# Revit family: Faucet-Deck_Mount-Bath-KOHLER-MODERN-K-97360T_2
name_source: partatom
category: Plumbing Fixtures
revit_build: Autodesk Revit 2017 (Build: 20160225_1515(x64)
units: mm (PartAtom-declared; Revit-internal decimal feet)

## family parameters
Cut with Voids When Loaded = No
Host = Face
OmniClass Number = 23.31.11.00
OmniClass Title = Faucets
Part Type = Normal
Room Calculation Point = No
Round Connector Dimension = Use Diameter
Shared = No

## types (6) — shared parameters
ADA Compliant = No
Assembly Code = D2010
CW Connection = Yes
Cold Water Inlet = Cold Water Inlet
Date Modified = 05/20/2020
Default Elevation = 36"
Drain Included = No
Flow Rate = 0 GPM
HW Connection = Yes
Handle Clearance = 3 3/8"
Height = 6 13/16"
Hot Water Inlet = Hot Water Inlet
Length = 7 13/16"
Manufacturer = KOHLER Co.
MasterFormat 1995 = 15410
MasterFormat 2004 = 22.41.39
Material = Premium Metal Construction
Pressure = 72.52 psi
Product Name = MODERN
Spout Reach = 7 13/16"
URL = http://www.kohler.com.cn
Vent Connection = No
Waste Connection = No
Waste Water Outlet = Waste Water Outlet
WaterSense Certified = No
Width = 2 9/16"

## per-type parameters (varying)
| type | Description | Finish | Height of Handshower | Model | Product Documentation Link | Product Page URL | Type |
| B4,TT-Vibrant Titanium | 3 hole cylinder side bathtub faucet | Kohler-Metal-TT-Vibrant_Titanium | 9 7/8" | K-97360T-B4-TT | http://files.kohler.com.cn | http://www.kohler.com.cn | 2 |
| 4E,CP-Polished Chrome | HOB MOUNT BATH SPOUT with Handshower | Kohler-Metal-CP-Polished_Chrome | 9 7/8" | K-97360T-4E-CP |  |  | 3 |
| 4E,TT-Vibrant Titanium | HOB MOUNT BATH SPOUT with Handshower | Kohler-Metal-TT-Vibrant_Titanium | 9 7/8" | K-97360T-4E-TT |  |  | 4 |
| B4,CP-Polished Chrome | 3 hole cylinder side bathtub faucet | Kohler-Metal-CP-Polished_Chrome | 9 7/8" | K-97360T-B4-CP | http://files.kohler.com.cn | http://www.kohler.com.cn | 1 |
| CP-Polished Chrome | HOB MOUNT BATH SPOUT with Handshower | Kohler-Metal-CP-Polished_Chrome | 9 1/8" | K-97360T-4-CP |  |  | 5 |
| TT-Vibrant Titanium | HOB MOUNT BATH SPOUT with Handshower | Kohler-Metal-TT-Vibrant_Titanium | 9 1/8" | K-97360T-4-TT |  |  | 6 |

## geometry (parser evidence)
native form markers: Sweep x12
no freeform markers — native parametric forms only
